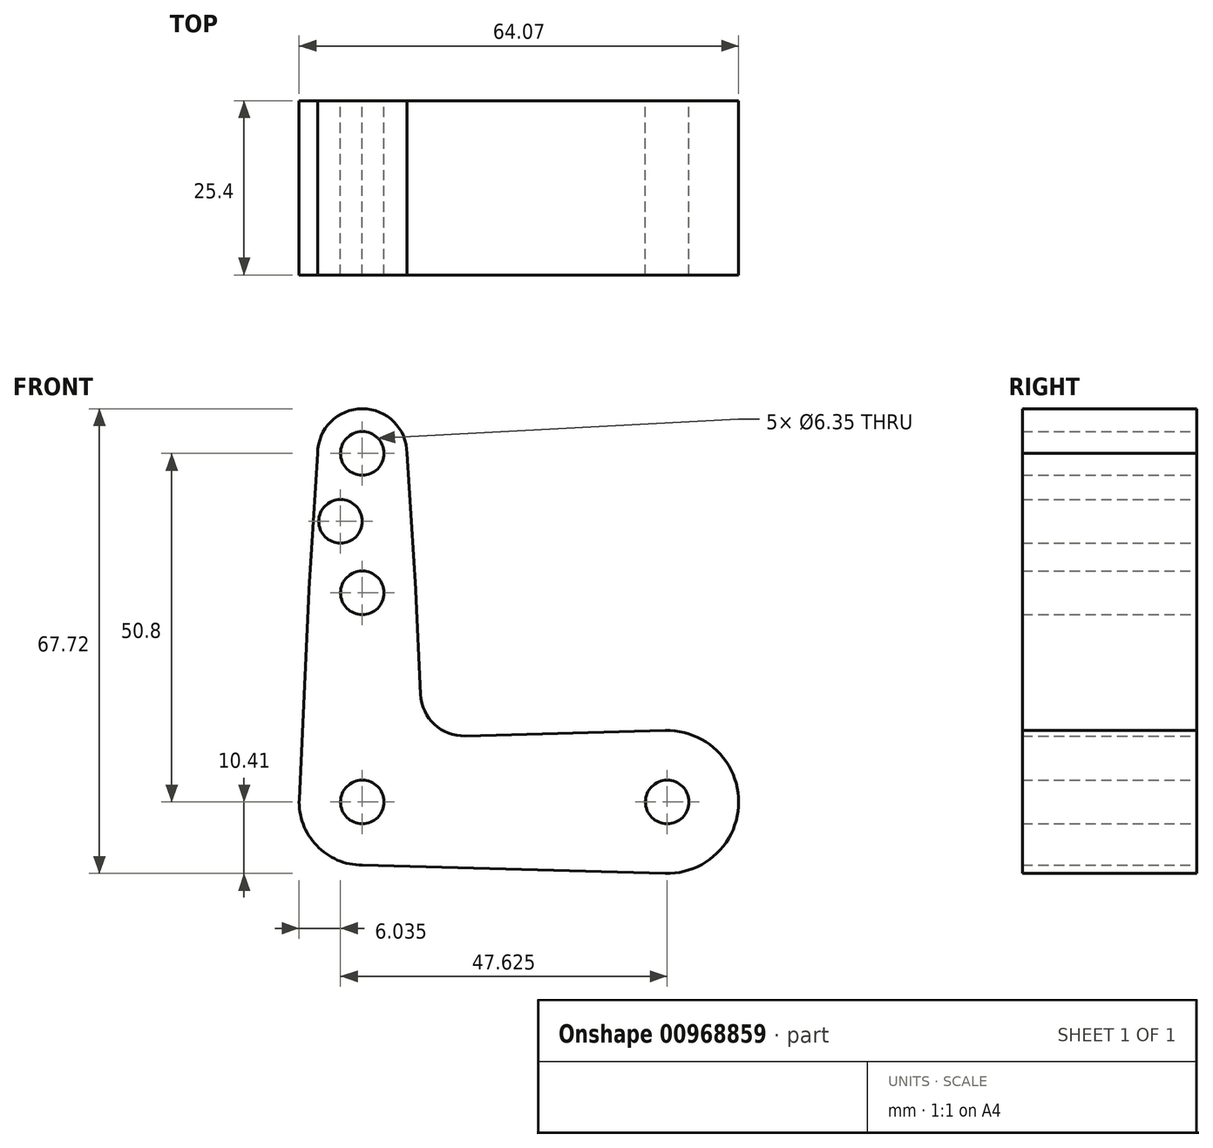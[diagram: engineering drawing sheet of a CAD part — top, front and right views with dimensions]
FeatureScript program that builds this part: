
annotation { "Feature Type Name" : "Feature", "Feature Type Description" : "" }
export const myFeature = defineFeature(function(context is Context, id is Id, definition is map)
    precondition{}
    {
        {
            var Q0;
            Q0=qCreatedBy(makeId("Front.planeOp"),FACE);
            var sketch = newSketch(context, id + "F0", { "sketchPlane" : qUnion([Q0])});
            skCircle(sketch, "E0", {"center": v(0, 50.8) * mm, "radius": 6.5 * mm});
            skCircle(sketch, "E1", {"center": v(0, 30.48) * mm, "radius": 7.8 * mm});
            skCircle(sketch, "E2", {"center": v(0, 0) * mm, "radius": 9.2 * mm});
            skCircle(sketch, "E3", {"center": v(44.45, 0) * mm, "radius": 10.4 * mm});
            skLineSegment(sketch, "E4", {"start": v(0, 50.8) * mm, "end": v(0, 0) * mm, "construction": true});
            skLineSegment(sketch, "E5", {"start": v(0, 0) * mm, "end": v(44.45, 0) * mm, "construction": true});
            skLineSegment(sketch, "E6", {"start": v(-6.5, 50.8) * mm, "end": v(-7.8, 30.99) * mm});
            skLineSegment(sketch, "E7", {"start": v(-7.8, 30.84) * mm, "end": v(-9.22, 0) * mm});
            skLineSegment(sketch, "E8", {"start": v(6.5, 50.8) * mm, "end": v(7.8, 30.99) * mm});
            skLineSegment(sketch, "E9", {"start": v(7.8, 30.84) * mm, "end": v(8.5, 15.67) * mm});
            skLineSegment(sketch, "E10", {"start": v(0, -9.2) * mm, "end": v(44.17, -10.4) * mm});
            skLineSegment(sketch, "E11", {"start": v(44.17, 10.4) * mm, "end": v(15.01, 9.62) * mm});
            skCircle(sketch, "E12", {"center": v(0, 50.8) * mm, "radius": 3.18 * mm});
            skCircle(sketch, "E13", {"center": v(0, 30.48) * mm, "radius": 3.18 * mm});
            skCircle(sketch, "E14", {"center": v(0, 0) * mm, "radius": 3.18 * mm});
            skCircle(sketch, "E15", {"center": v(44.45, 0) * mm, "radius": 3.18 * mm});
            skCircle(sketch, "E16", {"center": v(-3.17, 40.9) * mm, "radius": 3.18 * mm});
            skPoint(sketch, "E16.centerSnap0", {"position": v(-7.15, 40.9) * mm});
            skPoint(sketch, "E17.newPointA", {"position": v(0, 9.21) * mm});
            skPoint(sketch, "E17.newPointB", {"position": v(9.22, 0) * mm});
            skArc(sketch, "E17.filletArc", {"start": v(8.5, 15.67) * mm, "mid": v(10.52, 11.31) * mm, "end": v(15.01, 9.62) * mm});
            skSolve(sketch);
        }
        {
            var Q0;
            Q0=makeQuery(id+"F0.imprint","IMPRINT",FACE,{"disambiguationData":[TD([[makeQuery(id+"F0.imprint","IMPRINT",EDGE,{"derivedFrom":sQuery(id+"F0.wireOp",EDGE,"E12")}),-1.0]])]});
            var Q1;
            Q1=makeQuery(id+"F0.imprint","IMPRINT",FACE,{"disambiguationData":[TD([[makeQuery(id+"F0.imprint","IMPRINT",EDGE,{"derivedFrom":sQuery(id+"F0.wireOp",EDGE,"E14")}),-1.0]])]});
            var Q2;
            Q2=makeQuery(id+"F0.imprint","IMPRINT",FACE,{"disambiguationData":[TD([[makeQuery(id+"F0.imprint","IMPRINT",EDGE,{"derivedFrom":sQuery(id+"F0.wireOp",EDGE,"E15")}),-1.0]])]});
            var Q3;
            {var subQ0=sQuery(id+"F0.wireOp",EDGE,"E6");Q3=makeQuery(id+"F0.imprint","IMPRINT",FACE,{"disambiguationData":[TD([[makeQuery(id+"F0.imprint","IMPRINT",EDGE,{"derivedFrom":subQ0}),1.0]])]});}
            var Q4;
            Q4=makeQuery(id+"F0.imprint","IMPRINT",FACE,{"disambiguationData":[TD([[makeQuery(id+"F0.imprint","IMPRINT",EDGE,{"derivedFrom":sQuery(id+"F0.wireOp",EDGE,"E13")}),-1.0]])]});
            var Q5;
            {var subQ8=sQuery(id+"F0.wireOp",EDGE,"E9");Q5=makeQuery(id+"F0.imprint","IMPRINT",FACE,{"disambiguationData":[TD([[makeQuery(id+"F0.imprint","IMPRINT",EDGE,{"derivedFrom":subQ8}),-1.0]])]});}
            extrude(context, id + "F1", {"entities" : qUnion([Q0, Q1, Q2, Q3, Q4, Q5]), "depth" : 25.4 * mm, "offsetDistance" : 25.4 * mm});
        }
    });
